# Revit family: YA4025551_Ducha Monocontrol Yangzi Pro
name_source: partatom
category: Specialty Equipment
units: mm (PartAtom-declared; Revit-internal decimal feet)

## family parameters
Always vertical = Yes
Cut with Voids When Loaded = No
Part Type = Normal
Room Calculation Point = No
Round Connector Dimension = Use Diameter
Shared = No
Work Plane-Based = No

## types (1)
- YA4025551_Ducha Monocontrol Yangzi Pro
    Alto Grifo = 220 mm  [stored 0.721785 ft]
    Altura ducha = 6 mm  [stored 0.019685 ft]
    Ancho = 200 mm  [stored 0.656168 ft]
    Ancho Grifo = 125 mm  [stored 0.410105 ft]
    Capacidad de flujo = 12 L/min (2,5 gpm)
    Ciclo de vida de la unidad de cierre = 250.000 ciclos
    Creado por = IDD
    Fecha de creación = 30/07/2020
    Manufacturer = Corona
    Material = Corona_Cromado
    Model = Ducha Monocrontol Yangzi Pro
    Presion maxima = 860 kPa (125 psi)
    Presion minima = 138 kPa (20 psi)
    Profundidad = 500 mm  [stored 1.64042 ft]
    Resistencia al Torqué de Roscas Metálicas = (1/2), hasta 61 N-m (45 Lb-pie.)
    Resistencia de la Manija al Torque Maximo = 12 L/min (2,5 gpm)
    Temperatura de uso = De 4o C a 66o C (40o F y 150o F)

note: [stored X ft] marks values corroborated as IEEE doubles in the binary element streams (Revit-internal decimal feet)

## geometry (parser evidence)
native form markers: Sweep x2
no freeform markers — native parametric forms only
